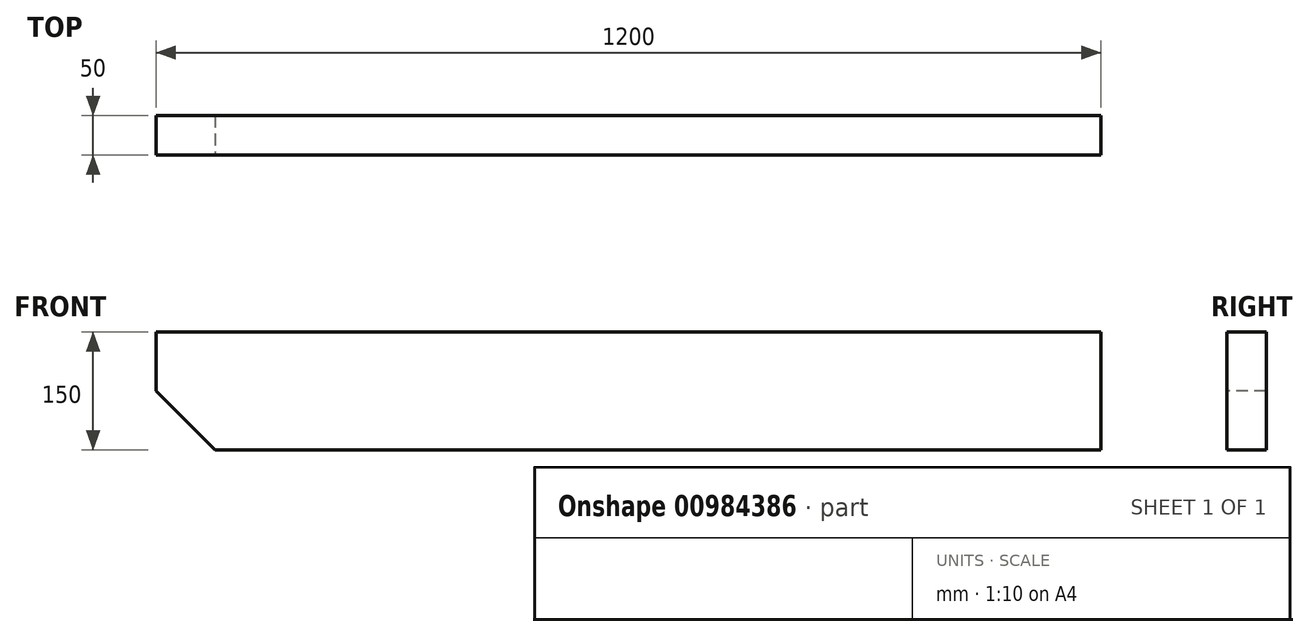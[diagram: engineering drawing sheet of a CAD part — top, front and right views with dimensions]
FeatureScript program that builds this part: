
annotation { "Feature Type Name" : "Feature", "Feature Type Description" : "" }
export const myFeature = defineFeature(function(context is Context, id is Id, definition is map)
    precondition{}
    {
        {
            var Q0;
            Q0=qCreatedBy(makeId("Right.planeOp"),FACE);
            var sketch = newSketch(context, id + "F0", { "sketchPlane" : qUnion([Q0])});
            skLineSegment(sketch, "E0.bottom", {"start": v(25, 75) * mm, "end": v(-25, 75) * mm});
            skLineSegment(sketch, "E0.top", {"start": v(25, -75) * mm, "end": v(-25, -75) * mm});
            skLineSegment(sketch, "E0.left", {"start": v(25, 75) * mm, "end": v(25, -75) * mm});
            skLineSegment(sketch, "E0.right", {"start": v(-25, 75) * mm, "end": v(-25, -75) * mm});
            skPoint(sketch, "E0.middle", {"position": v(0, 0) * mm});
            skSolve(sketch);
        }
        {
            var Q0;
            Q0=makeQuery(id+"F0.imprint","IMPRINT",FACE,{"disambiguationData":[TD([[makeQuery(id+"F0.imprint","IMPRINT",EDGE,{"derivedFrom":sQuery(id+"F0.wireOp",EDGE,"E0.bottom")}),1.0]])]});
            extrude(context, id + "F1", {"entities" : qUnion([Q0]), "endBound" : BoundingType.SYMMETRIC, "depth" : 1200 * mm, "offsetDistance" : 25 * mm});
        }
        {
            var Q0;
            Q0=makeQuery(id+"F1.opExtrude","SWEPT_FACE",FACE,{"disambiguationData":[OSD([sQuery(id+"F0.wireOp",EDGE,"E0.right")])]});
            var sketch = newSketch(context, id + "F2", { "sketchPlane" : qUnion([Q0])});
            skLineSegment(sketch, "E1", {"start": v(-600, 0) * mm, "end": v(-600, -75) * mm});
            skLineSegment(sketch, "E2", {"start": v(-600, -75) * mm, "end": v(-525, -75) * mm});
            skLineSegment(sketch, "E3", {"start": v(-600, 0) * mm, "end": v(-525, -75) * mm});
            skSolve(sketch);
        }
        {
            var Q0;
            Q0 = qSketchRegion(id + "F2", true);
            extrude(context, id + "F3", {"entities" : qUnion([Q0]), "operationType" : NewBodyOperationType.REMOVE, "endBound" : BoundingType.THROUGH_ALL, "oppositeDirection" : true, "depth" : 25 * mm, "offsetDistance" : 25 * mm});
        }
    });
